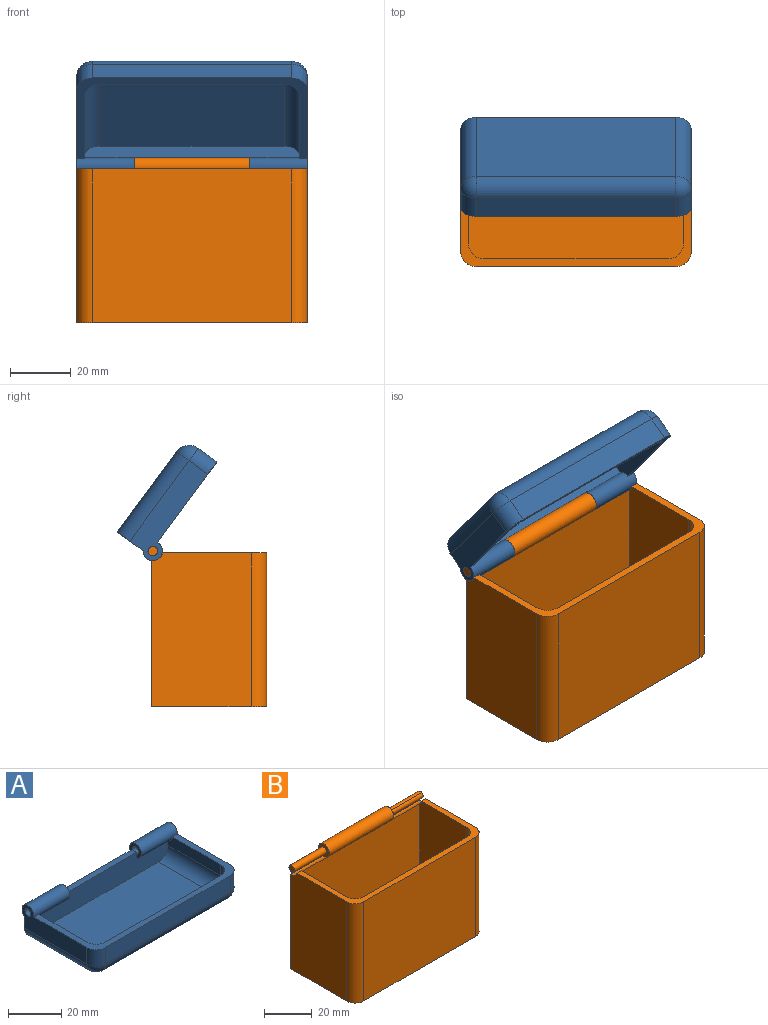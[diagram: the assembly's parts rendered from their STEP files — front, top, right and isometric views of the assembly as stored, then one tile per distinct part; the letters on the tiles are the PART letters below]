
ASSEMBLY  parts=2 mates=1
PART A: 34 faces, bbox 76.2x39.4x16.4 mm
  f0: plane 38.1x2.54mm, normal (0,0,1), area 96.8mm2, adj f1,f5,f14,f15,f18,f19
  f1: plane 71.12x10.16mm, normal (0,-1,0), area 624.5mm2, adj f0,f8,f9,f11,f12,f14,f15,f16
  f2: plane 34.34x11.27mm, normal (-1,0,0), area 264.3mm2, adj f3,f5,f16,f17,f20,f29
  f3: plane 76.2x33.11mm, normal (0,0,1), area 348.8mm2, adj f2,f4,f6,f8,f9,f10,f12,f16
  f4: plane 34.35x11.25mm, normal (1,0,0), area 264.2mm2, adj f3,f5,f12,f13,f21,f33
  f5: plane 76.2x12.7mm, normal (0,1,0), area 876.1mm2, adj f0,f2,f4,f7,f12,f14,f16,f18
  f6: plane 66.04x7.62mm, normal (0,-1,0), area 503.2mm2, adj f3,f20,f21,f31
  f7: plane 66.04x33.02mm, normal (0,0,-1), area 2180.6mm2, adj f5,f29,f31,f33
  f8: plane 27.94x5.08mm, normal (-1,0,0), area 137.3mm2, adj f1,f3,f12,f23,f28
  f9: plane 27.94x5.08mm, normal (1,0,0), area 137.4mm2, adj f1,f3,f16,f22,f24
  f10: plane 60.96x5.08mm, normal (0,1,0), area 309.7mm2, adj f3,f22,f23,f26
  f11: plane 60.96x27.94mm, normal (0,0,1), area 1703.2mm2, adj f1,f24,f26,f28
  f12: cylinder r=3.17mm len=19.05mm, axis (1,0,0), area 319.4mm2, adj f1,f3,f4,f5,f8,f14
  f13: cylinder r=1.59mm len=19.05mm, axis (1,0,0), area 190mm2, adj f4,f14,f15
  f14: plane 6.35x6.27mm, normal (-1,0,0), area 19.2mm2, adj f0,f1,f5,f12,f13
  f15: plane 2.21x1.13mm, normal (1,0,0), area 2mm2, adj f0,f1,f13
  f16: cylinder r=3.17mm len=19.05mm, axis (-1,0,0), area 319.5mm2, adj f1,f2,f3,f5,f9,f18
  f17: cylinder r=1.59mm len=19.05mm, axis (-1,0,0), area 190mm2, adj f2,f18,f19
  f18: plane 6.35x6.27mm, normal (1,0,0), area 19.2mm2, adj f0,f1,f5,f16,f17
  f19: plane 2.2x1.11mm, normal (-1,0,0), area 2mm2, adj f0,f1,f17
  f20: cylinder r=5.08mm len=7.62mm, axis (0,0,1), area 60.8mm2, adj f2,f3,f6,f30
  f21: cylinder r=5.08mm len=7.62mm, axis (0,0,-1), area 60.8mm2, adj f3,f4,f6,f32
  f22: cylinder r=5.08mm len=5.08mm, axis (0,0,-1), area 40.5mm2, adj f3,f9,f10,f25
  f23: cylinder r=5.08mm len=5.08mm, axis (0,0,1), area 40.5mm2, adj f3,f8,f10,f27
  f24: cylinder r=5.08mm len=27.94mm, axis (0,1,0), area 223mm2, adj f1,f9,f11,f25
  f25: sphere r=5.08mm, area 40.5mm2, adj f22,f24,f26
  f26: cylinder r=5.08mm len=60.96mm, axis (-1,0,0), area 486.4mm2, adj f10,f11,f25,f27
  f27: sphere r=5.08mm, area 40.5mm2, adj f23,f26,f28
  f28: cylinder r=5.08mm len=27.94mm, axis (0,-1,0), area 223mm2, adj f1,f8,f11,f27
  f29: cylinder r=5.08mm len=33.02mm, axis (0,-1,0), area 263.5mm2, adj f2,f5,f7,f30
  f30: sphere r=5.08mm, area 40.5mm2, adj f20,f29,f31
  f31: cylinder r=5.08mm len=66.04mm, axis (1,0,0), area 527mm2, adj f6,f7,f30,f32
  f32: sphere r=5.08mm, area 40.5mm2, adj f21,f31,f33
  f33: cylinder r=5.08mm len=33.02mm, axis (0,1,0), area 263.5mm2, adj f4,f5,f7,f32
PART B: 25 faces, bbox 76.2x40.8x54.6 mm
  f0: plane 3.18x3.18mm, normal (-1,0,0), area 7.9mm2, adj f16
  f1: plane 76.2x34.47mm, normal (0,0,1), area 355.7mm2, adj f3,f6,f7,f9,f10,f11,f18,f20
  f2: plane 76.2x48.26mm, normal (0,1,0), area 3677.1mm2, adj f3,f6,f8,f13,f14,f18,f20
  f3: plane 50.8x33.02mm, normal (1,0,0), area 1670mm2, adj f1,f2,f8,f18,f22
  f4: plane 71.12x46.41mm, normal (0,-1,0), area 3299.7mm2, adj f9,f10,f12,f13,f14,f18,f20
  f5: plane 3.17x3.16mm, normal (1,0,0), area 7.9mm2, adj f17,f19
  f6: plane 50.8x33.02mm, normal (-1,0,0), area 1670mm2, adj f1,f2,f8,f20,f21
  f7: plane 66.04x50.8mm, normal (0,-1,0), area 3354.8mm2, adj f1,f8,f21,f22
  f8: plane 76.2x38.1mm, normal (0,0,-1), area 2892.1mm2, adj f2,f3,f6,f7,f21,f22
  f9: plane 48.26x27.94mm, normal (-1,0,0), area 1347.1mm2, adj f1,f4,f12,f18,f24
  f10: plane 48.26x27.94mm, normal (1,0,0), area 1347.1mm2, adj f1,f4,f12,f20,f23
  f11: plane 60.96x48.26mm, normal (0,1,0), area 2941.9mm2, adj f1,f12,f23,f24
  f12: plane 71.12x33.02mm, normal (0,0,1), area 2337.3mm2, adj f4,f9,f10,f11,f23,f24
  f13: cylinder r=3.17mm len=38.1mm, axis (-1,0,0), area 656.8mm2, adj f2,f4,f14,f15
  f14: plane 6.35x6.34mm, normal (1,0,0), area 23.8mm2, adj f2,f4,f13,f17,f18,f19
  f15: plane 6.35x6.35mm, normal (-1,0,0), area 23.8mm2, adj f13,f16,f20
  f16: cylinder r=1.59mm len=19.05mm, axis (-1,0,0), area 190mm2, adj f0,f15
  f17: cylinder r=1.59mm len=19.05mm, axis (-1,0,0), area 94.8mm2, adj f5,f14,f19
  f18: cylinder r=3.17mm len=19.05mm, axis (-1,0,0), area 57.3mm2, adj f1,f2,f3,f4,f9,f14
  f19: cylinder r=1.59mm len=19.05mm, axis (-1,0,0), area 94.8mm2, adj f5,f14,f17
  f20: cylinder r=3.17mm len=19.05mm, axis (1,0,0), area 57.3mm2, adj f1,f2,f4,f6,f10,f15
  f21: cylinder r=5.08mm len=50.8mm, axis (0,0,1), area 405.4mm2, adj f1,f6,f7,f8
  f22: cylinder r=5.08mm len=50.8mm, axis (0,0,-1), area 405.4mm2, adj f1,f3,f7,f8
  f23: cylinder r=5.08mm len=48.26mm, axis (0,0,-1), area 385.1mm2, adj f1,f10,f11,f12
  f24: cylinder r=5.08mm len=48.26mm, axis (0,0,1), area 385.1mm2, adj f1,f9,f11,f12
PLACE A rot(axis=(0,-0.89,0.45),180deg) t=(41.82,-33.29,53.1)mm
PLACE B rot(axis=(0,1,0),0deg) t=(41.82,-47.11,9.22)mm fixed
MATE revolute B.f18 <-> A.f16  axis (-1,0,0) through (79.92,-28.58,35.21)mm
